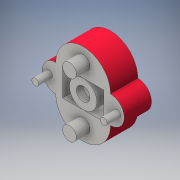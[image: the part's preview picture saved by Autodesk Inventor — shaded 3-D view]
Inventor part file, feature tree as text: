
AUTODESK INVENTOR PART (.ipt)
format: ipt  version: 2016 (Build 200138000, 138)  size: 213,504 bytes
history: native  units: in
note: dims shown in document units (in); Inventor stores cm internally (conversion verified against a paired STEP export)
features: sketch x8, extrude x7, hole x1
ambient origin geometry x8: Origin, YZ Plane, XZ Plane, XY Plane, X Axis, Y Axis, Z Axis, Center Point
bodies: Solid1 (feature_tree)
feature tree (16):
  extrude  "Extrusion1"  Depth=1.0in
  extrude  "Extrusion2"  Depth=0.25in
  extrude  "Extrusion3"  Depth=0.25in
  extrude  "Extrusion4"  Depth=0.25in TaperAngle=0.0deg
  hole  "Hole1"  [1 undecoded]
  extrude  "Extrusion7"  Depth=0.125in
  extrude  "Extrusion8"  Depth=0.25in
  extrude  "Extrusion9"  Depth=0.125in TaperAngle=0.0deg
  sketch  "Sketch1"  dims[d0=0.5in d1=1.0in]
  sketch  "Sketch2"  dims[d2=0.5in d3=0.0in d4=0.25in]
  sketch  "Sketch3"  dims[d5=0.25in d6=0.25in]
  sketch  "Sketch4"  dims[d7=0.25in d8=0.25in d9=0.0in]
  sketch  "Sketch7"  dims[d10=0.125in d11=0.125in]
  sketch  "Sketch8"  dims[d12=0.125in d13=0.125in]
  sketch  "Sketch9"  dims[d14=0.25in d15=0.0in d16=0.25in]
  sketch  "Sketch10"  dims[d17=0.25in d18=0.0in d23=0.25in d24=0.75in d25=0.375in d26=0.375in d27=0.5635in d28=1.0in d29=0.8108in d30=0.125in d31=0.0in d32=0.125in d33=0.0in d34=0.05in d35=0.0in]
note: 1 required parameter value undecoded (feature->parameter linkage not recoverable at this tier; creation-order binding heuristic only, values carry confidence <= 0.55)
